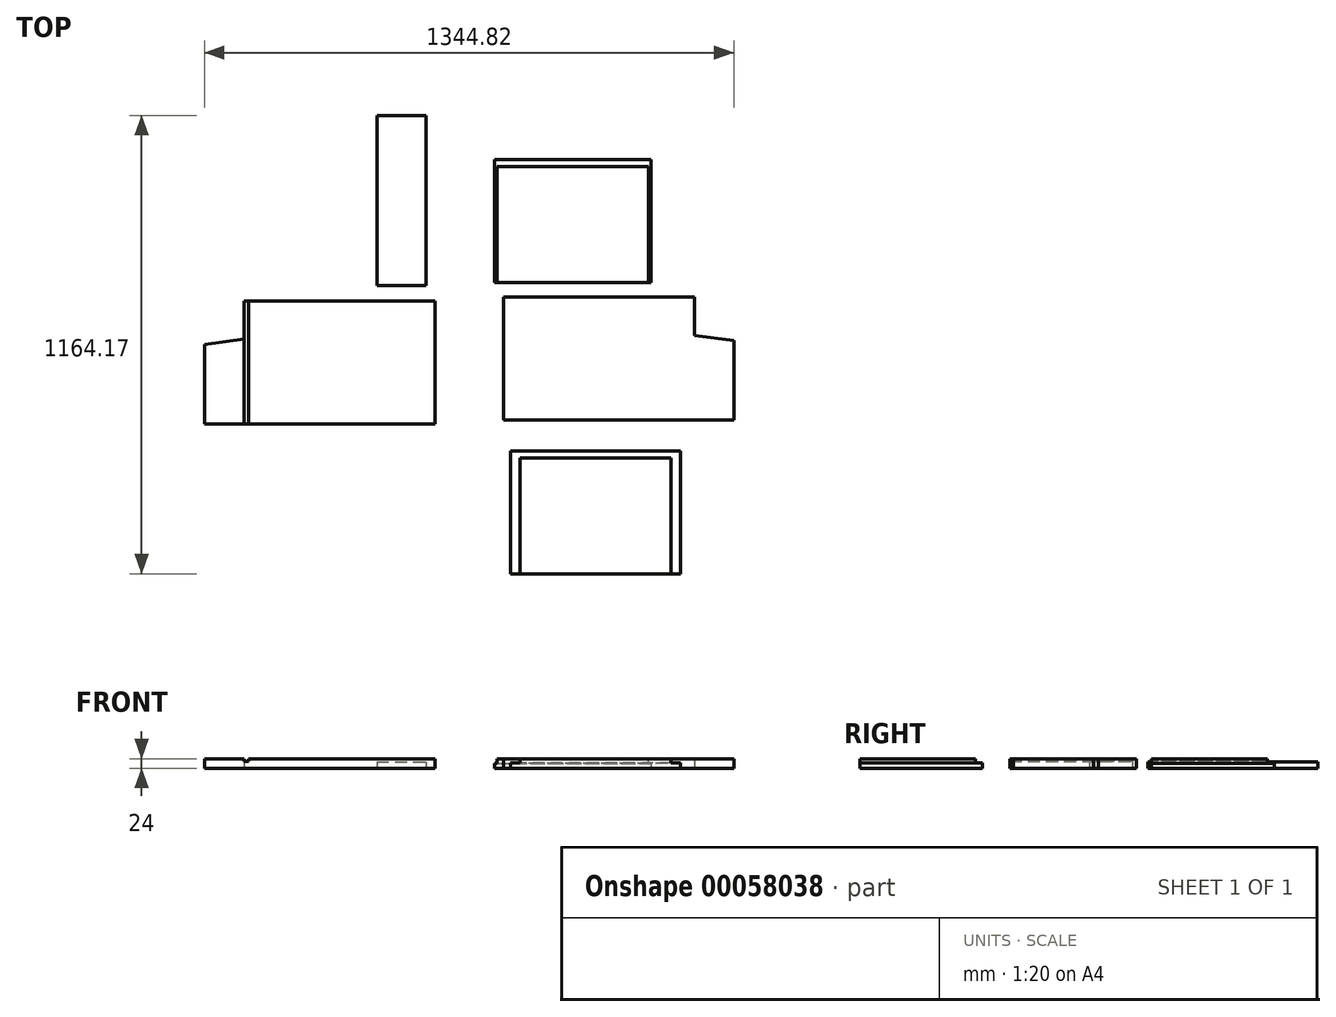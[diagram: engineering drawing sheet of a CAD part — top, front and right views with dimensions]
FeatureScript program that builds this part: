
annotation { "Feature Type Name" : "Feature", "Feature Type Description" : "" }
export const myFeature = defineFeature(function(context is Context, id is Id, definition is map)
    precondition{}
    {
        {
            var Q0;
            Q0=qCreatedBy(makeId("Top.planeOp"),FACE);
            var sketch = newSketch(context, id + "F0", { "sketchPlane" : qUnion([Q0]), "disableImprinting" : false});
            skLineSegment(sketch, "E0", {"start": v(-303.7, -112.43) * mm, "end": v(281.3, -112.43) * mm});
            skLineSegment(sketch, "E1", {"start": v(281.3, -112.43) * mm, "end": v(281.3, 89.57) * mm});
            skLineSegment(sketch, "E2", {"start": v(281.3, 89.57) * mm, "end": v(181.3, 102.57) * mm});
            skLineSegment(sketch, "E3", {"start": v(181.3, 102.57) * mm, "end": v(181.3, 199.57) * mm});
            skLineSegment(sketch, "E4", {"start": v(181.3, 199.57) * mm, "end": v(-303.7, 199.57) * mm});
            skLineSegment(sketch, "E5", {"start": v(-303.7, 199.57) * mm, "end": v(-303.7, -112.43) * mm});
            skSolve(sketch);
        }
        {
            var Q0;
            Q0=makeQuery(id+"F0.imprint","IMPRINT",FACE,{"disambiguationData":[TD([[makeQuery(id+"F0.imprint","IMPRINT",EDGE,{"derivedFrom":sQuery(id+"F0.wireOp",EDGE,"E0")}),1.0]])]});
            extrude(context, id + "F1", {"entities" : qUnion([Q0]), "flatOperationType" : FlatOperationType.REMOVE, "offsetDistance" : 25 * mm, "depth" : 24 * mm, "domain" : OperationDomain.MODEL});
        }
        {
            var Q0;
            Q0=makeQuery(id+"F1.opExtrude","CAP_FACE",FACE,{"disambiguationData":[OSD([sQuery(id+"F0.wireOp",EDGE,"E0"),sQuery(id+"F0.wireOp",EDGE,"E1"),sQuery(id+"F0.wireOp",EDGE,"E2"),sQuery(id+"F0.wireOp",EDGE,"E3"),sQuery(id+"F0.wireOp",EDGE,"E4"),sQuery(id+"F0.wireOp",EDGE,"E5")])],"isStart":true});
            var sketch = newSketch(context, id + "F2", { "sketchPlane" : qUnion([Q0]), "disableImprinting" : false});
            skLineSegment(sketch, "E6.bottom", {"start": v(-327.06, -549.54) * mm, "end": v(70.94, -549.54) * mm});
            skLineSegment(sketch, "E6.top", {"start": v(-327.06, -237.54) * mm, "end": v(70.94, -237.54) * mm});
            skLineSegment(sketch, "E6.left", {"start": v(-327.06, -549.54) * mm, "end": v(-327.06, -237.54) * mm});
            skLineSegment(sketch, "E6.right", {"start": v(70.94, -549.54) * mm, "end": v(70.94, -237.54) * mm});
            skSolve(sketch);
        }
        {
            var Q0;
            Q0=makeQuery(id+"F2.imprint","IMPRINT",FACE,{"disambiguationData":[TD([[makeQuery(id+"F2.imprint","IMPRINT",EDGE,{"derivedFrom":sQuery(id+"F2.wireOp",EDGE,"E6.bottom")}),1.0]])]});
            extrude(context, id + "F3", {"entities" : qUnion([Q0]), "oppositeDirection" : true, "depth" : 24 * mm});
        }
        {
            var Q0;
            Q0=makeQuery(id+"F3.opExtrude","CAP_FACE",FACE,{"disambiguationData":[OSD([sQuery(id+"F2.wireOp",EDGE,"E6.bottom"),sQuery(id+"F2.wireOp",EDGE,"E6.top"),sQuery(id+"F2.wireOp",EDGE,"E6.left"),sQuery(id+"F2.wireOp",EDGE,"E6.right")])],"isStart":false});
            var sketch = newSketch(context, id + "F4", { "sketchPlane" : qUnion([Q0]), "disableImprinting" : false});
            skLineSegment(sketch, "E7", {"start": v(-327.06, 549.54) * mm, "end": v(-327.06, 237.54) * mm});
            skLineSegment(sketch, "E8", {"start": v(-327.06, 237.54) * mm, "end": v(-320.06, 237.54) * mm});
            skLineSegment(sketch, "E9", {"start": v(-320.06, 237.54) * mm, "end": v(-320.06, 531.54) * mm});
            skLineSegment(sketch, "E10", {"start": v(-320.06, 531.54) * mm, "end": v(63.94, 531.54) * mm});
            skLineSegment(sketch, "E11", {"start": v(63.94, 531.54) * mm, "end": v(63.94, 237.54) * mm});
            skLineSegment(sketch, "E12", {"start": v(63.94, 237.54) * mm, "end": v(70.94, 237.54) * mm});
            skLineSegment(sketch, "E13", {"start": v(70.94, 237.54) * mm, "end": v(70.94, 549.54) * mm});
            skLineSegment(sketch, "E14", {"start": v(70.94, 549.54) * mm, "end": v(-327.06, 549.54) * mm});
            skSolve(sketch);
        }
        {
            var Q0;
            Q0 = qSketchRegion(id + "F4", true);
            extrude(context, id + "F5", {"entities" : qUnion([Q0]), "operationType" : NewBodyOperationType.REMOVE, "flatOperationType" : FlatOperationType.REMOVE, "oppositeDirection" : true, "offsetDistance" : 25 * mm, "depth" : 12 * mm, "domain" : OperationDomain.MODEL});
        }
        {
            var Q0;
            Q0=qCreatedBy(makeId("Top.planeOp"),FACE);
            var sketch = newSketch(context, id + "F6", { "sketchPlane" : qUnion([Q0]), "disableImprinting" : false});
            skLineSegment(sketch, "E15.bottom", {"start": v(-285.92, -191.18) * mm, "end": v(146.08, -191.18) * mm});
            skLineSegment(sketch, "E15.top", {"start": v(-285.92, -503.18) * mm, "end": v(146.08, -503.18) * mm});
            skLineSegment(sketch, "E15.left", {"start": v(-285.92, -191.18) * mm, "end": v(-285.92, -503.18) * mm});
            skLineSegment(sketch, "E15.right", {"start": v(146.08, -191.18) * mm, "end": v(146.08, -503.18) * mm});
            skSolve(sketch);
        }
        {
            var Q0;
            Q0=makeQuery(id+"F6.imprint","IMPRINT",FACE,{"disambiguationData":[TD([[makeQuery(id+"F6.imprint","IMPRINT",EDGE,{"derivedFrom":sQuery(id+"F6.wireOp",EDGE,"E15.bottom")}),-1.0]])]});
            extrude(context, id + "F7", {"entities" : qUnion([Q0]), "depth" : 24 * mm});
        }
        {
            var Q0;
            Q0=makeQuery(id+"F7.opExtrude","CAP_FACE",FACE,{"disambiguationData":[OSD([sQuery(id+"F6.wireOp",EDGE,"E15.bottom"),sQuery(id+"F6.wireOp",EDGE,"E15.top"),sQuery(id+"F6.wireOp",EDGE,"E15.left"),sQuery(id+"F6.wireOp",EDGE,"E15.right")])],"isStart":false});
            var sketch = newSketch(context, id + "F8", { "sketchPlane" : qUnion([Q0])});
            skLineSegment(sketch, "E16", {"start": v(-285.92, -503.18) * mm, "end": v(-285.92, -191.18) * mm});
            skLineSegment(sketch, "E17", {"start": v(-285.92, -191.18) * mm, "end": v(146.08, -191.18) * mm});
            skLineSegment(sketch, "E18", {"start": v(146.08, -191.18) * mm, "end": v(146.08, -503.18) * mm});
            skLineSegment(sketch, "E19", {"start": v(146.08, -503.18) * mm, "end": v(122.08, -503.18) * mm});
            skLineSegment(sketch, "E20", {"start": v(122.08, -503.18) * mm, "end": v(122.08, -209.18) * mm});
            skLineSegment(sketch, "E21", {"start": v(122.08, -209.18) * mm, "end": v(-261.92, -209.18) * mm});
            skLineSegment(sketch, "E22", {"start": v(-261.92, -209.18) * mm, "end": v(-261.92, -503.18) * mm});
            skLineSegment(sketch, "E23", {"start": v(-261.92, -503.18) * mm, "end": v(-285.92, -503.18) * mm});
            skSolve(sketch);
        }
        {
            var Q0;
            Q0 = qSketchRegion(id + "F8", true);
            extrude(context, id + "F9", {"entities" : qUnion([Q0]), "operationType" : NewBodyOperationType.REMOVE, "flatOperationType" : FlatOperationType.REMOVE, "oppositeDirection" : true, "offsetDistance" : 25 * mm, "depth" : 10 * mm, "domain" : OperationDomain.MODEL});
        }
        {
            var Q0;
            Q0=qCreatedBy(makeId("Top.planeOp"),FACE);
            var sketch = newSketch(context, id + "F10", { "sketchPlane" : qUnion([Q0])});
            skLineSegment(sketch, "E24.bottom", {"start": v(-625.6, 660.99) * mm, "end": v(-500.6, 660.99) * mm});
            skLineSegment(sketch, "E24.top", {"start": v(-625.6, 228.99) * mm, "end": v(-500.6, 228.99) * mm});
            skLineSegment(sketch, "E24.left", {"start": v(-625.6, 660.99) * mm, "end": v(-625.6, 228.99) * mm});
            skLineSegment(sketch, "E24.right", {"start": v(-500.6, 660.99) * mm, "end": v(-500.6, 228.99) * mm});
            skSolve(sketch);
        }
        {
            var Q0;
            Q0=makeQuery(id+"F10.imprint","IMPRINT",FACE,{"disambiguationData":[TD([[makeQuery(id+"F10.imprint","IMPRINT",EDGE,{"derivedFrom":sQuery(id+"F10.wireOp",EDGE,"E24.bottom")}),-1.0]])]});
            extrude(context, id + "F11", {"entities" : qUnion([Q0]), "depth" : 16 * mm});
        }
        {
            var Q0;
            Q0=qCreatedBy(makeId("Top.planeOp"),FACE);
            var sketch = newSketch(context, id + "F12", { "sketchPlane" : qUnion([Q0]), "disableImprinting" : false});
            skLineSegment(sketch, "E25", {"start": v(-963.5, 189.8) * mm, "end": v(-478.5, 189.8) * mm});
            skLineSegment(sketch, "E26", {"start": v(-478.5, -122.2) * mm, "end": v(-1063.5, -122.2) * mm});
            skLineSegment(sketch, "E27", {"start": v(-1063.5, -122.2) * mm, "end": v(-1063.5, 79.8) * mm});
            skLineSegment(sketch, "E28", {"start": v(-1063.5, 79.8) * mm, "end": v(-963.5, 92.8) * mm});
            skLineSegment(sketch, "E29", {"start": v(-963.5, 189.8) * mm, "end": v(-963.5, 92.8) * mm});
            skLineSegment(sketch, "E30", {"start": v(-478.5, 189.8) * mm, "end": v(-478.5, -122.2) * mm});
            skSolve(sketch);
        }
        {
            var Q0;
            Q0=makeQuery(id+"F12.imprint","IMPRINT",FACE,{"disambiguationData":[TD([[makeQuery(id+"F12.imprint","IMPRINT",EDGE,{"derivedFrom":sQuery(id+"F12.wireOp",EDGE,"E25")}),-1.0]])]});
            extrude(context, id + "F13", {"entities" : qUnion([Q0]), "flatOperationType" : FlatOperationType.REMOVE, "offsetDistance" : 25 * mm, "depth" : 24 * mm, "domain" : OperationDomain.MODEL});
        }
        {
            var Q0;
            Q0=makeQuery(id+"F13.opExtrude","CAP_FACE",FACE,{"disambiguationData":[OSD([sQuery(id+"F12.wireOp",EDGE,"E25"),sQuery(id+"F12.wireOp",EDGE,"E26"),sQuery(id+"F12.wireOp",EDGE,"E27"),sQuery(id+"F12.wireOp",EDGE,"E28"),sQuery(id+"F12.wireOp",EDGE,"E29"),sQuery(id+"F12.wireOp",EDGE,"E30")])],"isStart":false});
            var sketch = newSketch(context, id + "F14", { "sketchPlane" : qUnion([Q0]), "disableImprinting" : false});
            skLineSegment(sketch, "E31", {"start": v(-963.5, 189.8) * mm, "end": v(-963.5, -122.2) * mm});
            skLineSegment(sketch, "E32", {"start": v(-963.5, -122.2) * mm, "end": v(-951.5, -122.2) * mm});
            skLineSegment(sketch, "E33", {"start": v(-951.5, -122.2) * mm, "end": v(-951.5, 189.8) * mm});
            skLineSegment(sketch, "E34", {"start": v(-951.5, 189.8) * mm, "end": v(-963.5, 189.8) * mm});
            skSolve(sketch);
        }
        {
            var Q0;
            Q0 = qSketchRegion(id + "F14", true);
            extrude(context, id + "F15", {"entities" : qUnion([Q0]), "operationType" : NewBodyOperationType.REMOVE, "flatOperationType" : FlatOperationType.REMOVE, "oppositeDirection" : true, "offsetDistance" : 25 * mm, "depth" : 7 * mm, "domain" : OperationDomain.MODEL});
        }
    });
